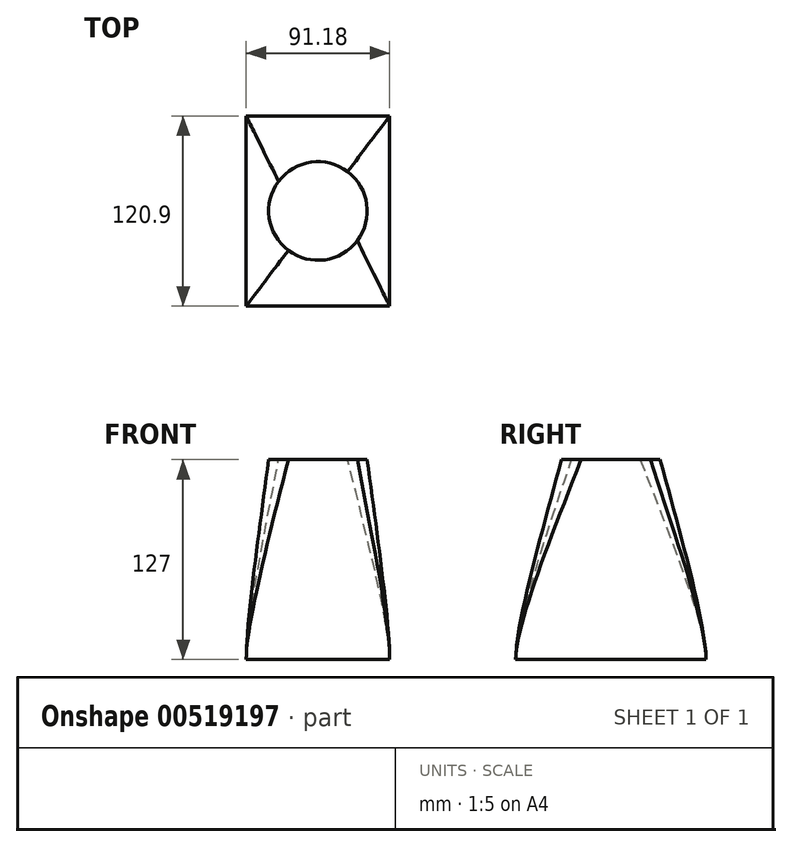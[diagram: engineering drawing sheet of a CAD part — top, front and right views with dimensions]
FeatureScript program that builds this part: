
annotation { "Feature Type Name" : "Feature", "Feature Type Description" : "" }
export const myFeature = defineFeature(function(context is Context, id is Id, definition is map)
    precondition{}
    {
        {
            var Q0;
            Q0=qCreatedBy(makeId("Top.planeOp"),FACE);
            var sketch = newSketch(context, id + "F0", { "sketchPlane" : qUnion([Q0])});
            skLineSegment(sketch, "E0.bottom", {"start": v(45.59, 60.45) * mm, "end": v(-45.59, 60.45) * mm});
            skLineSegment(sketch, "E0.top", {"start": v(45.59, -60.45) * mm, "end": v(-45.59, -60.45) * mm});
            skLineSegment(sketch, "E0.left", {"start": v(45.59, 60.45) * mm, "end": v(45.59, -60.45) * mm});
            skLineSegment(sketch, "E0.right", {"start": v(-45.59, 60.45) * mm, "end": v(-45.59, -60.45) * mm});
            skPoint(sketch, "E0.middle", {"position": v(0, 0) * mm});
            skSolve(sketch);
        }
        {
            var Q0;
            Q0=qCreatedBy(makeId("Top.planeOp"),FACE);
            cPlane(context, id + "F1", {"entities" : qUnion([Q0]), "cplaneType" : CPlaneType.OFFSET, "offset" : 127 * mm, "width" : 152.4 * mm, "height" : 152.4 * mm});
        }
        {
            var Q0;
            Q0=qCreatedBy(id+"F1.planeOp",FACE);
            var sketch = newSketch(context, id + "F2", { "sketchPlane" : qUnion([Q0])});
            skPoint(sketch, "E1.middle", {"position": v(0, 0) * mm});
            skCircle(sketch, "E2", {"center": v(0, 0) * mm, "radius": 31.3 * mm});
            skSolve(sketch);
        }
        {
            var Q0;
            Q0=makeQuery(id+"F0.imprint","IMPRINT",FACE,{"disambiguationData":[TD([[makeQuery(id+"F0.imprint","IMPRINT",EDGE,{"derivedFrom":sQuery(id+"F0.wireOp",EDGE,"E0.bottom")}),1.0]])]});
            var Q1;
            Q1=makeQuery(id+"F2.imprint","IMPRINT",FACE,{"disambiguationData":[TD([[makeQuery(id+"F2.imprint","IMPRINT",EDGE,{"derivedFrom":sQuery(id+"F2.wireOp",EDGE,"E2")}),1.0]])]});
            var Q2;
            Q2=sQuery(id+"F2.wireOp",EDGE,"E2");
            loft(context, id + "F3", {"startCondition" : LoftEndDerivativeType.NORMAL_TO_PROFILE, "startMagnitude" : 0.5, "sheetProfilesArray" : [{ "sheetProfileEntities" : qUnion([Q0]) }, { "sheetProfileEntities" : qUnion([Q1]) }], "guidesArray" : [{ "guideEntities" : qUnion([Q2]), "guideDerivativeType" : LoftGuideDerivativeType.DEFAULT, "guideDerivativeMagnitude" : 1 }]});
        }
    });
